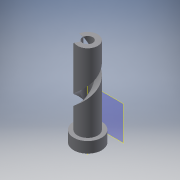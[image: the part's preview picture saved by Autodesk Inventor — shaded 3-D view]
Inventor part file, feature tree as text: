
AUTODESK INVENTOR PART (.ipt)
format: ipt  version: 2018 (Build 220112000, 112)  size: 205,312 bytes
history: native  units: mm
features: sketch x8, extrude x7, plane x1, other x1, helix x1
ambient origin geometry x8: Origin, YZ Plane, XZ Plane, XY Plane, X Axis, Y Axis, Z Axis, Center Point
bodies: Solid1 (feature_tree)
feature tree (18):
  extrude  "Extrusion1"  Depth=3.0mm
  extrude  "Extrusion2"  Depth=18.0mm
  extrude  "Extrusion3"  Depth=7.0mm
  extrude  "Extrusion5"  Depth=1.0mm
  plane  "Work Plane1"
  extrude  "Extrusion8"  Depth=6.5mm
  sketch  "Sketch9"  dims[d34=12.0mm d44=6.0mm]
  other  "Work Axis1"
  helix  "Coil2"  [1 undecoded]
  extrude  "Extrusión9"  Depth=6.0mm
  extrude  "Extrusión10"  Depth=5.0mm
  sketch  "Sketch1"  dims[d0=6.0mm d1=3.0mm]
  sketch  "Sketch2"  dims[d2=80.0mm d4=360.0deg d6=18.0mm]
  sketch  "Sketch3"  dims[d7=7.0mm d8=0.0mm d9=13.0mm]
  sketch  "Sketch5"  dims[d10=1.0mm d11=0.0mm d12=13.0mm]
  sketch  "Sketch8"  dims[d13=50.0mm d14=0.0mm d25=6.5mm d26=6.0mm d27=0.0mm]
  sketch  "Boceto13"  dims[d45=4.5mm d46=0.0mm d61=5.0mm]
  sketch  "Boceto14"  dims[d62=7.0mm d63=35.0mm d64=50.0mm d65=40.0mm d66=0.174533mm d67=90.0deg d68=90.0deg d69=0.0mm d70=0.0mm d72=7.0mm d73=0.0mm d74=2.0mm d75=0.0mm]
note: 1 required parameter value undecoded (feature->parameter linkage not recoverable at this tier; creation-order binding heuristic only, values carry confidence <= 0.55)
